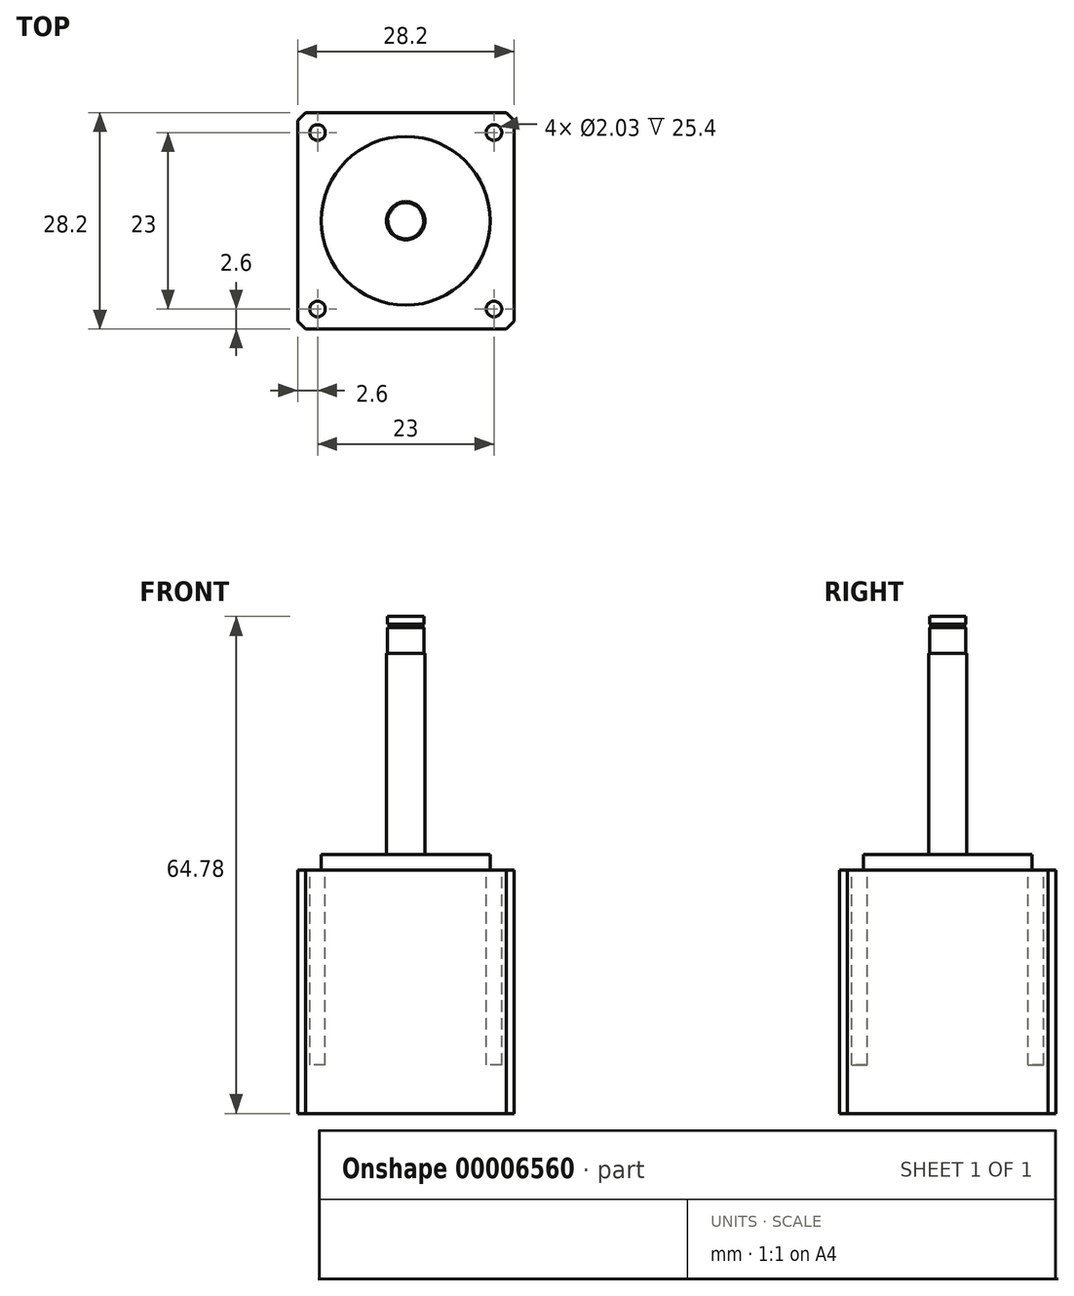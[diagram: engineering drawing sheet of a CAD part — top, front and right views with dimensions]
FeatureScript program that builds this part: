
annotation { "Feature Type Name" : "Feature", "Feature Type Description" : "" }
export const myFeature = defineFeature(function(context is Context, id is Id, definition is map)
    precondition{}
    {
        {
            var Q0;
            Q0=qCreatedBy(makeId("Top.planeOp"),FACE);
            var sketch = newSketch(context, id + "F0", { "sketchPlane" : qUnion([Q0])});
            skLineSegment(sketch, "E0.rect.bottom", {"start": v(14.1, -14.1) * mm, "end": v(-14.1, -14.1) * mm});
            skLineSegment(sketch, "E0.rect.top", {"start": v(14.1, 14.1) * mm, "end": v(-14.1, 14.1) * mm});
            skLineSegment(sketch, "E0.rect.left", {"start": v(14.1, -14.1) * mm, "end": v(14.1, 14.1) * mm});
            skLineSegment(sketch, "E0.rect.right", {"start": v(-14.1, -14.1) * mm, "end": v(-14.1, 14.1) * mm});
            skPoint(sketch, "E0.rect.middle", {"position": v(0, 0) * mm});
            skSolve(sketch);
        }
        {
            var Q0;
            Q0=makeQuery(id+"F0.imprint","IMPRINT",FACE,{"disambiguationData":[TD([[makeQuery(id+"F0.imprint","IMPRINT",EDGE,{"derivedFrom":sQuery(id+"F0.wireOp",EDGE,"E0.rect.bottom")}),-1.0]])]});
            extrude(context, id + "F1", {"entities" : qUnion([Q0]), "depth" : 31.75 * mm});
        }
        {
            var Q0;
            Q0=makeQuery(id+"F1.opExtrude","CAP_FACE",FACE,{"disambiguationData":[OSD([sQuery(id+"F0.wireOp",EDGE,"E0.rect.bottom"),sQuery(id+"F0.wireOp",EDGE,"E0.rect.top"),sQuery(id+"F0.wireOp",EDGE,"E0.rect.left"),sQuery(id+"F0.wireOp",EDGE,"E0.rect.right")])],"isStart":false});
            var sketch = newSketch(context, id + "F2", { "sketchPlane" : qUnion([Q0])});
            skCircle(sketch, "E1", {"center": v(0, 0) * mm, "radius": 11 * mm});
            skSolve(sketch);
        }
        {
            var Q0;
            Q0=makeQuery(id+"F2.imprint","IMPRINT",FACE,{"disambiguationData":[TD([[makeQuery(id+"F2.imprint","IMPRINT",EDGE,{"derivedFrom":sQuery(id+"F2.wireOp",EDGE,"E1")}),1.0]])]});
            extrude(context, id + "F3", {"entities" : qUnion([Q0]), "operationType" : NewBodyOperationType.ADD, "depth" : 1.98 * mm});
        }
        {
            var Q0;
            Q0=makeQuery(id+"F3.opExtrude","CAP_FACE",FACE,{"disambiguationData":[OSD([sQuery(id+"F2.wireOp",EDGE,"E1")])],"isStart":false});
            var sketch = newSketch(context, id + "F4", { "sketchPlane" : qUnion([Q0])});
            skCircle(sketch, "E2", {"center": v(0, 0) * mm, "radius": 2.5 * mm});
            skSolve(sketch);
        }
        {
            var Q0;
            Q0 = qSketchRegion(id + "F4", true);
            extrude(context, id + "F5", {"entities" : qUnion([Q0]), "operationType" : NewBodyOperationType.ADD, "depth" : 26.5 * mm - 0.25 * mm});
        }
        {
            var Q0;
            Q0=makeQuery(id+"F1.opExtrude","SWEPT_EDGE",EDGE,{"disambiguationData":[OSD([sQuery(id+"F0.wireOp",EDGE,"E0.rect.top"),sQuery(id+"F0.wireOp",EDGE,"E0.rect.left")])]});
            var Q1;
            Q1=makeQuery(id+"F1.opExtrude","SWEPT_EDGE",EDGE,{"disambiguationData":[OSD([sQuery(id+"F0.wireOp",EDGE,"E0.rect.top"),sQuery(id+"F0.wireOp",EDGE,"E0.rect.right")])]});
            var Q2;
            Q2=makeQuery(id+"F1.opExtrude","SWEPT_EDGE",EDGE,{"disambiguationData":[OSD([sQuery(id+"F0.wireOp",EDGE,"E0.rect.bottom"),sQuery(id+"F0.wireOp",EDGE,"E0.rect.left")])]});
            var Q3;
            Q3=makeQuery(id+"F1.opExtrude","SWEPT_EDGE",EDGE,{"disambiguationData":[OSD([sQuery(id+"F0.wireOp",EDGE,"E0.rect.bottom"),sQuery(id+"F0.wireOp",EDGE,"E0.rect.right")])]});
            chamfer(context, id + "F6", {"entities" : qUnion([Q0, Q1, Q2, Q3]), "width" : 1.02 * mm, "tangentPropagation" : true});
        }
        {
            var Q0;
            Q0=makeQuery(id+"F1.opExtrude","CAP_FACE",FACE,{"disambiguationData":[OSD([sQuery(id+"F0.wireOp",EDGE,"E0.rect.bottom"),sQuery(id+"F0.wireOp",EDGE,"E0.rect.top"),sQuery(id+"F0.wireOp",EDGE,"E0.rect.left"),sQuery(id+"F0.wireOp",EDGE,"E0.rect.right")])],"isStart":false});
            var sketch = newSketch(context, id + "F7", { "sketchPlane" : qUnion([Q0])});
            skLineSegment(sketch, "E3.rect.bottom", {"start": v(11.5, 11.5) * mm, "end": v(-11.5, 11.5) * mm});
            skLineSegment(sketch, "E3.rect.top", {"start": v(11.5, -11.5) * mm, "end": v(-11.5, -11.5) * mm});
            skLineSegment(sketch, "E3.rect.left", {"start": v(11.5, 11.5) * mm, "end": v(11.5, -11.5) * mm});
            skLineSegment(sketch, "E3.rect.right", {"start": v(-11.5, 11.5) * mm, "end": v(-11.5, -11.5) * mm});
            skPoint(sketch, "E3.rect.middle", {"position": v(0, 0) * mm});
            skPoint(sketch, "E4", {"position": v(-11.5, 11.5) * mm});
            skPoint(sketch, "E5", {"position": v(11.5, 11.5) * mm});
            skPoint(sketch, "E6", {"position": v(11.5, -11.5) * mm});
            skPoint(sketch, "E7", {"position": v(-11.5, -11.5) * mm});
            skCircle(sketch, "E8", {"center": v(-11.5, 11.5) * mm, "radius": 1.02 * mm});
            skCircle(sketch, "E9", {"center": v(11.5, 11.5) * mm, "radius": 1.02 * mm});
            skCircle(sketch, "E10", {"center": v(11.5, -11.5) * mm, "radius": 1.02 * mm});
            skCircle(sketch, "E11", {"center": v(-11.5, -11.5) * mm, "radius": 1.02 * mm});
            skSolve(sketch);
        }
        {
            var Q0;
            {var subQ0=sQuery(id+"F7.wireOp",EDGE,"E3.rect.left");var subQ3=sQuery(id+"F7.wireOp",EDGE,"E3.rect.bottom");var subQ4=makeQuery(id+"F7.imprint","INTERSECT",VERTEX,{"derivedFrom":[subQ3,subQ0]});Q0=makeQuery(id+"F7.imprint","IMPRINT",FACE,{"disambiguationData":[TD([[makeQuery(id+"F7.imprint","IMPRINT",EDGE,{"disambiguationData":[TD([[subQ4,-1.0]])],"derivedFrom":subQ3}),-1.0]])]});}
            var Q1;
            {var subQ1=sQuery(id+"F7.wireOp",EDGE,"E3.rect.left");var subQ3=sQuery(id+"F7.wireOp",EDGE,"E3.rect.bottom");var subQ5=makeQuery(id+"F7.imprint","INTERSECT",VERTEX,{"derivedFrom":[subQ3,subQ1]});Q1=makeQuery(id+"F7.imprint","IMPRINT",FACE,{"disambiguationData":[TD([[makeQuery(id+"F7.imprint","IMPRINT",EDGE,{"disambiguationData":[TD([[subQ5,-1.0]])],"derivedFrom":subQ3}),1.0]])]});}
            var Q2;
            {var subQ1=sQuery(id+"F7.wireOp",EDGE,"E3.rect.right");var subQ3=sQuery(id+"F7.wireOp",EDGE,"E3.rect.bottom");var subQ5=makeQuery(id+"F7.imprint","INTERSECT",VERTEX,{"derivedFrom":[subQ3,subQ1]});Q2=makeQuery(id+"F7.imprint","IMPRINT",FACE,{"disambiguationData":[TD([[makeQuery(id+"F7.imprint","IMPRINT",EDGE,{"disambiguationData":[TD([[subQ5,1.0]])],"derivedFrom":subQ3}),-1.0]])]});}
            var Q3;
            {var subQ1=sQuery(id+"F7.wireOp",EDGE,"E3.rect.right");var subQ3=sQuery(id+"F7.wireOp",EDGE,"E3.rect.bottom");var subQ5=makeQuery(id+"F7.imprint","INTERSECT",VERTEX,{"derivedFrom":[subQ3,subQ1]});Q3=makeQuery(id+"F7.imprint","IMPRINT",FACE,{"disambiguationData":[TD([[makeQuery(id+"F7.imprint","IMPRINT",EDGE,{"disambiguationData":[TD([[subQ5,1.0]])],"derivedFrom":subQ3}),1.0]])]});}
            var Q4;
            {var subQ1=sQuery(id+"F7.wireOp",EDGE,"E3.rect.left");var subQ3=sQuery(id+"F7.wireOp",EDGE,"E3.rect.top");var subQ5=makeQuery(id+"F7.imprint","INTERSECT",VERTEX,{"derivedFrom":[subQ3,subQ1]});Q4=makeQuery(id+"F7.imprint","IMPRINT",FACE,{"disambiguationData":[TD([[makeQuery(id+"F7.imprint","IMPRINT",EDGE,{"disambiguationData":[TD([[subQ5,-1.0]])],"derivedFrom":subQ3}),1.0]])]});}
            var Q5;
            {var subQ1=sQuery(id+"F7.wireOp",EDGE,"E3.rect.left");var subQ3=sQuery(id+"F7.wireOp",EDGE,"E3.rect.top");var subQ5=makeQuery(id+"F7.imprint","INTERSECT",VERTEX,{"derivedFrom":[subQ3,subQ1]});Q5=makeQuery(id+"F7.imprint","IMPRINT",FACE,{"disambiguationData":[TD([[makeQuery(id+"F7.imprint","IMPRINT",EDGE,{"disambiguationData":[TD([[subQ5,-1.0]])],"derivedFrom":subQ3}),-1.0]])]});}
            var Q6;
            {var subQ1=sQuery(id+"F7.wireOp",EDGE,"E3.rect.right");var subQ3=sQuery(id+"F7.wireOp",EDGE,"E3.rect.top");var subQ5=makeQuery(id+"F7.imprint","INTERSECT",VERTEX,{"derivedFrom":[subQ3,subQ1]});Q6=makeQuery(id+"F7.imprint","IMPRINT",FACE,{"disambiguationData":[TD([[makeQuery(id+"F7.imprint","IMPRINT",EDGE,{"disambiguationData":[TD([[subQ5,1.0]])],"derivedFrom":subQ3}),1.0]])]});}
            var Q7;
            {var subQ1=sQuery(id+"F7.wireOp",EDGE,"E3.rect.right");var subQ3=sQuery(id+"F7.wireOp",EDGE,"E3.rect.top");var subQ5=makeQuery(id+"F7.imprint","INTERSECT",VERTEX,{"derivedFrom":[subQ3,subQ1]});Q7=makeQuery(id+"F7.imprint","IMPRINT",FACE,{"disambiguationData":[TD([[makeQuery(id+"F7.imprint","IMPRINT",EDGE,{"disambiguationData":[TD([[subQ5,1.0]])],"derivedFrom":subQ3}),-1.0]])]});}
            extrude(context, id + "F8", {"entities" : qUnion([Q0, Q1, Q2, Q3, Q4, Q5, Q6, Q7]), "operationType" : NewBodyOperationType.REMOVE, "oppositeDirection" : true, "depth" : 25.4 * mm});
        }
        {
            var Q0;
            Q0=makeQuery(id+"F5.opExtrude","CAP_FACE",FACE,{"disambiguationData":[OSD([sQuery(id+"F4.wireOp",EDGE,"E2")])],"isStart":false});
            var sketch = newSketch(context, id + "F9", { "sketchPlane" : qUnion([Q0])});
            skCircle(sketch, "E12.0", {"center": v(0, 0) * mm, "radius": 2.5 * mm});
            skCircle(sketch, "E13.0", {"center": v(0, 0) * mm, "radius": 2.37 * mm});
            skSolve(sketch);
        }
        {
            var Q0;
            Q0=makeQuery(id+"F9.imprint","IMPRINT",FACE,{"disambiguationData":[TD([[makeQuery(id+"F9.imprint","IMPRINT",EDGE,{"derivedFrom":sQuery(id+"F9.wireOp",EDGE,"E13.0")}),1.0]])]});
            extrude(context, id + "F10", {"entities" : qUnion([Q0]), "operationType" : NewBodyOperationType.ADD, "depth" : 3.1 * mm + 0.25 * mm});
        }
        {
            var Q0;
            Q0=makeQuery(id+"F10.opExtrude","CAP_FACE",FACE,{"disambiguationData":[OSD([sQuery(id+"F9.wireOp",EDGE,"E13.0")])],"isStart":false});
            var sketch = newSketch(context, id + "F11", { "sketchPlane" : qUnion([Q0])});
            skCircle(sketch, "E14.0", {"center": v(0, 0) * mm, "radius": 2.37 * mm});
            skCircle(sketch, "E15", {"center": v(0, 0) * mm, "radius": 2.22 * mm});
            skSolve(sketch);
        }
        {
            var Q0;
            Q0=makeQuery(id+"F11.imprint","IMPRINT",FACE,{"disambiguationData":[TD([[makeQuery(id+"F11.imprint","IMPRINT",EDGE,{"derivedFrom":sQuery(id+"F11.wireOp",EDGE,"E15")}),1.0]])]});
            extrude(context, id + "F12", {"entities" : qUnion([Q0]), "operationType" : NewBodyOperationType.ADD, "depth" : 0.46 * mm});
        }
        {
            var Q0;
            Q0=makeQuery(id+"F12.opExtrude","CAP_FACE",FACE,{"disambiguationData":[OSD([sQuery(id+"F11.wireOp",EDGE,"E15")])],"isStart":false});
            var sketch = newSketch(context, id + "F13", { "sketchPlane" : qUnion([Q0])});
            skCircle(sketch, "E16.0", {"center": v(0, 0) * mm, "radius": 2.22 * mm});
            skCircle(sketch, "E17.0", {"center": v(0, 0) * mm, "radius": 2.37 * mm});
            skSolve(sketch);
        }
        {
            var Q0;
            Q0=makeQuery(id+"F13.imprint","IMPRINT",FACE,{"disambiguationData":[TD([[makeQuery(id+"F13.imprint","IMPRINT",EDGE,{"derivedFrom":sQuery(id+"F13.wireOp",EDGE,"E16.0")}),1.0]])]});
            var Q1;
            Q1=makeQuery(id+"F13.imprint","IMPRINT",FACE,{"disambiguationData":[TD([[makeQuery(id+"F13.imprint","IMPRINT",EDGE,{"derivedFrom":sQuery(id+"F13.wireOp",EDGE,"E16.0")}),-1.0]])]});
            extrude(context, id + "F14", {"entities" : qUnion([Q0, Q1]), "operationType" : NewBodyOperationType.ADD, "depth" : 1 * mm});
        }
    });
